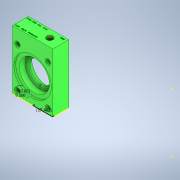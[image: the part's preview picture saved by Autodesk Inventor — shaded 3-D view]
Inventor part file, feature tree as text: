
AUTODESK INVENTOR PART (.ipt)
format: ipt  version: 2020 (Build 240168000, 168)  size: 551,424 bytes
history: native  units: in
note: dims shown in document units (in); Inventor stores cm internally (conversion verified against a paired STEP export)
features: sketch x4, hole x4, extrude x3, imported_body x1
ambient origin geometry x8: Origin, YZ Plane, XZ Plane, XY Plane, X Axis, Y Axis, Z Axis, Center Point
bodies: Solid1 (feature_tree)
feature tree (12):
  extrude  "Extrusion1"  Depth=0.3937in TaperAngle=0.0deg
  extrude  "Extrusion2"  Depth=0.3743in
  sketch  "Sketch3"  dims[d11=0.213in d12=0.2362in d13=0.4375in d14=0.25in d15=0.563in d16=0.375in d17=0.0in d18=0.3743in]
  hole  "Hole1"  [1 undecoded]
  hole  "Hole2"  [1 undecoded]
  hole  "Hole3"  [1 undecoded]
  hole  "Hole4"  [1 undecoded]
  extrude  "Extrusion3"  [1 undecoded]
  sketch  "Sketch1"  dims[d0=0.6398in d1=0.0in d2=0.3937in d3=0.0in]
  sketch  "Sketch2"  dims[d4=0.04in d5=0.2362in d6=0.4375in d7=0.25in d8=0.563in d9=0.9843in d10=0.8108in]
  sketch  "Sketch5"  dims[d19=0.0in d20=0.213in d21=0.2362in d22=0.4375in d23=0.25in d24=0.563in d25=0.25in d26=0.0in d27=0.04in d28=0.2362in d29=0.4375in d30=0.25in d31=0.563in d32=1.0in d33=0.8108in d34=0.1181in d35=0.0in d36=0.6875in]
  imported_body  "Base1"
note: 5 required parameter values undecoded (feature->parameter linkage not recoverable at this tier; creation-order binding heuristic only, values carry confidence <= 0.55)
